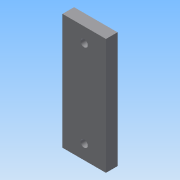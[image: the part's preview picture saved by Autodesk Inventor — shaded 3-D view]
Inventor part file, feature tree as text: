
AUTODESK INVENTOR PART (.ipt)
format: ipt  version: 2015 (Build 190159000, 159)  size: 76,800 bytes
history: native  units: mm
features: extrude x1, sketch x1
ambient origin geometry x8: Origin, YZ Plane, XZ Plane, XY Plane, X Axis, Y Axis, Z Axis, Center Point
bodies: Body1 (feature_tree)
feature tree (2):
  extrude  "Extrusion2"  Depth=30.0mm
  sketch  "Sketch1"  dims[d0=80.0mm d1=30.0mm d4=5.0mm d5=5.0mm d6=60.0mm d7=15.0mm d8=10.0mm d9=8.0mm d10=0.0mm]
